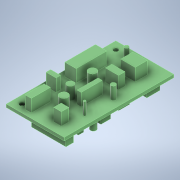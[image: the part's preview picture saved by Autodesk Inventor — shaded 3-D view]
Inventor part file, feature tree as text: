
AUTODESK INVENTOR PART (.ipt)
format: ipt  version: 2022 (Build 260153000, 153)  size: 239,616 bytes
history: native  units: mm
features: extrude x4, sketch x4
ambient origin geometry x8: Origin, YZ Plane, XZ Plane, XY Plane, X Axis, Y Axis, Z Axis, Center Point
bodies: Solid1 (feature_tree)
feature tree (8):
  extrude  "Extrusion1"  Depth=70.0mm
  extrude  "Extrusion2"  Depth=2.0mm
  extrude  "Extrusion3"  Depth=5.0mm
  extrude  "Extrusion4"  Depth=7.0mm
  sketch  "Sketch1"  dims[d0=37.0mm d1=70.0mm]
  sketch  "Sketch2"  dims[d2=2.0mm d3=0.0mm d4=3.0mm]
  sketch  "Sketch3"  dims[d5=3.0mm d6=5.0mm]
  sketch  "Sketch4"  dims[d9=0.0mm d10=0.0mm d11=60.0mm d12=5.0mm d13=8.0mm d14=0.0mm d15=7.0mm d16=0.0mm]
